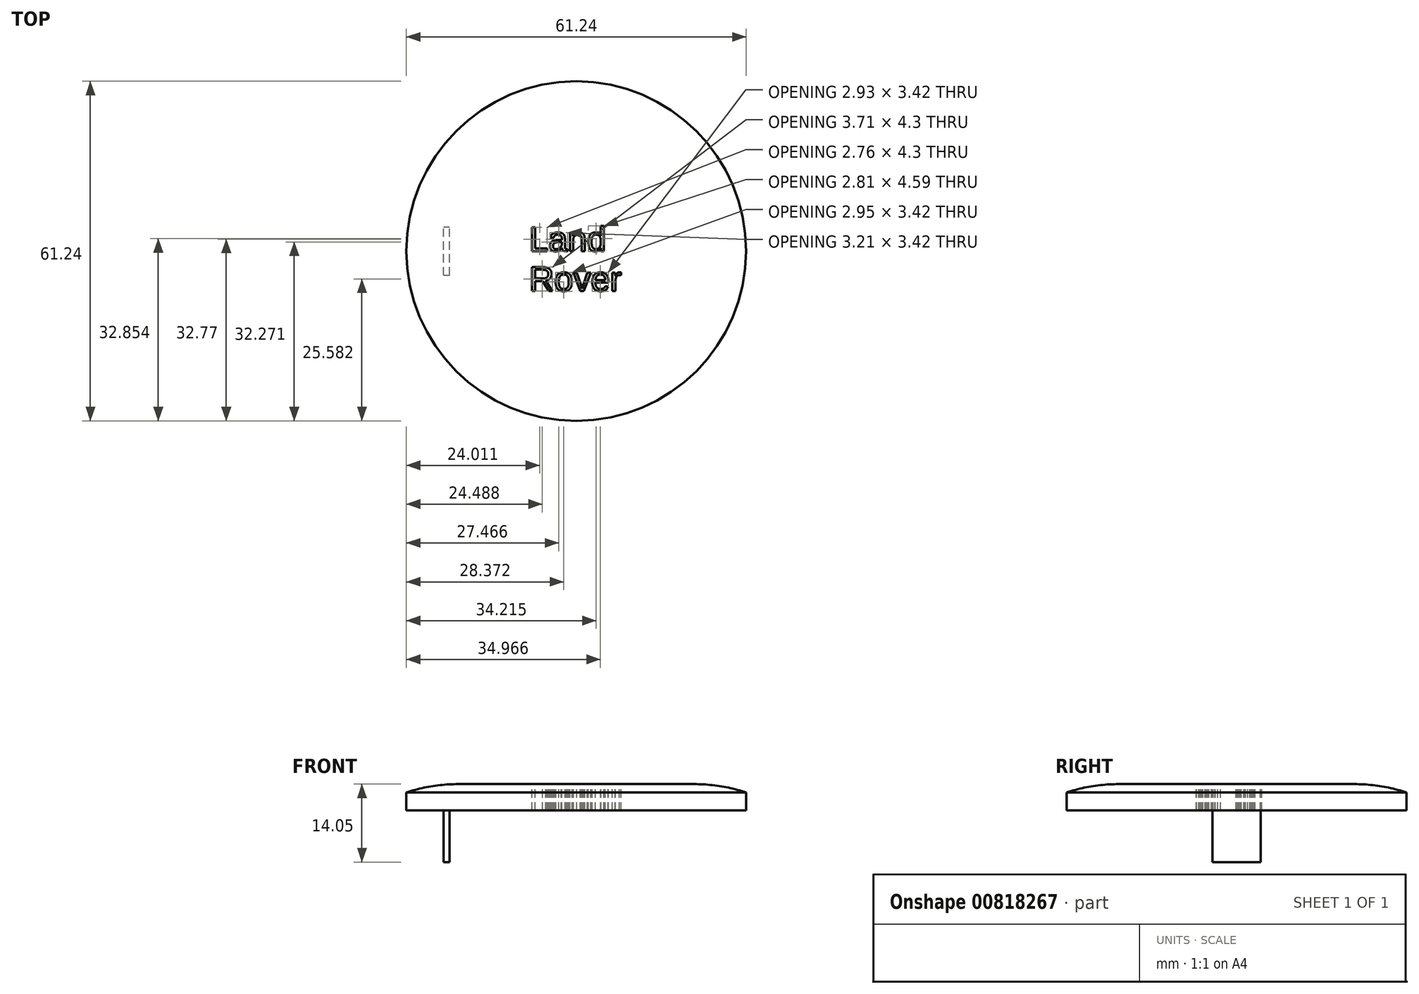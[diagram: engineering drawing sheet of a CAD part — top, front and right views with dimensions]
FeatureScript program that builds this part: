
annotation { "Feature Type Name" : "Feature", "Feature Type Description" : "" }
export const myFeature = defineFeature(function(context is Context, id is Id, definition is map)
    precondition{}
    {
        {
            var Q0;
            Q0=qCreatedBy(makeId("Top.planeOp"),FACE);
            var sketch = newSketch(context, id + "F0", { "sketchPlane" : qUnion([Q0])});
            skCircle(sketch, "E0", {"center": v(0, 0) * mm, "radius": 30.62 * mm});
            skSolve(sketch);
        }
        {
            var Q0;
            Q0=makeQuery(id+"F0.imprint","IMPRINT",FACE,{"disambiguationData":[TD([[makeQuery(id+"F0.imprint","IMPRINT",EDGE,{"derivedFrom":sQuery(id+"F0.wireOp",EDGE,"E0")}),1.0]])]});
            extrude(context, id + "F1", {"entities" : qUnion([Q0]), "depth" : 1.5 * mm, "offsetDistance" : 25 * mm});
        }
        {
            var Q0;
            Q0=makeQuery(id+"F1.opExtrude","CAP_FACE",FACE,{"disambiguationData":[OSD([sQuery(id+"F0.wireOp",EDGE,"E0")])],"isStart":false});
            fillet(context, id + "F2", {"entities" : qUnion([Q0]), "radius" : 30 * mm, "tangentPropagation" : true, "allowEdgeOverflow" : false});
        }
        {
            var Q0;
            Q0=makeQuery(id+"F1.opExtrude","CAP_FACE",FACE,{"disambiguationData":[OSD([sQuery(id+"F0.wireOp",EDGE,"E0")])],"isStart":true});
            var sketch = newSketch(context, id + "F3", { "sketchPlane" : qUnion([Q0])});
            skCircle(sketch, "E1.0", {"center": v(0, 0) * mm, "radius": 30.62 * mm});
            skSolve(sketch);
        }
        {
            var Q0;
            Q0=makeQuery(id+"F3.imprint","IMPRINT",FACE,{"disambiguationData":[TD([[makeQuery(id+"F3.imprint","IMPRINT",EDGE,{"derivedFrom":sQuery(id+"F3.wireOp",EDGE,"E1.0")}),-1.0]])]});
            extrude(context, id + "F4", {"entities" : qUnion([Q0]), "operationType" : NewBodyOperationType.ADD, "depth" : 3.25 * mm, "offsetDistance" : 25 * mm});
        }
        {
            var Q0;
            Q0=makeQuery(id+"F4.opExtrude","CAP_FACE",FACE,{"disambiguationData":[OSD([sQuery(id+"F3.wireOp",EDGE,"E1.0")])],"isStart":false});
            var sketch = newSketch(context, id + "F5", { "sketchPlane" : qUnion([Q0])});
            skLineSegment(sketch, "E2.bottom", {"start": v(-23.95, 4.35) * mm, "end": v(-22.85, 4.35) * mm});
            skLineSegment(sketch, "E2.top", {"start": v(-23.95, -4.35) * mm, "end": v(-22.85, -4.35) * mm});
            skLineSegment(sketch, "E2.left", {"start": v(-23.95, 4.35) * mm, "end": v(-23.95, -4.35) * mm});
            skLineSegment(sketch, "E2.right", {"start": v(-22.85, 4.35) * mm, "end": v(-22.85, -4.35) * mm});
            skPoint(sketch, "E2.middle", {"position": v(-23.4, 0) * mm});
            skPoint(sketch, "E3", {"position": v(0, -3.68) * mm});
            skSolve(sketch);
        }
        {
            var Q0;
            Q0 = qSketchRegion(id + "F5", true);
            extrude(context, id + "F6", {"entities" : qUnion([Q0]), "operationType" : NewBodyOperationType.ADD, "depth" : 9.3 * mm, "offsetDistance" : 25 * mm});
        }
        {
            var Q0;
            Q0=qCreatedBy(makeId("Right.planeOp"),FACE);
            var sketch = newSketch(context, id + "F7", { "sketchPlane" : qUnion([Q0])});
            skLineSegment(sketch, "E4", {"start": v(0, 0) * mm, "end": v(0, -19.14) * mm});
            skSolve(sketch);
        }
        {
            var Q0;
            Q0=makeQuery(id+"F1.opExtrude","CAP_FACE",FACE,{"disambiguationData":[OSD([sQuery(id+"F0.wireOp",EDGE,"E0")])],"isStart":false});
            var sketch = newSketch(context, id + "F8", { "sketchPlane" : qUnion([Q0])});
            skText(sketch, "E5", { "text": "Land \nRover", "fontName": "Arimo-Regular.ttf"});
            const initialGuessF8  = {"E5": [-0.0085, 0, 1, 0, 0.0045]};
            skSetInitialGuess(sketch, initialGuessF8);
            skSolve(sketch);
        }
        {
            var Q0;
            Q0 = qSketchRegion(id + "F8", true);
            extrude(context, id + "F9", {"entities" : qUnion([Q0]), "operationType" : NewBodyOperationType.REMOVE, "oppositeDirection" : true, "depth" : 5 * mm, "offsetDistance" : 25 * mm});
        }
    });
